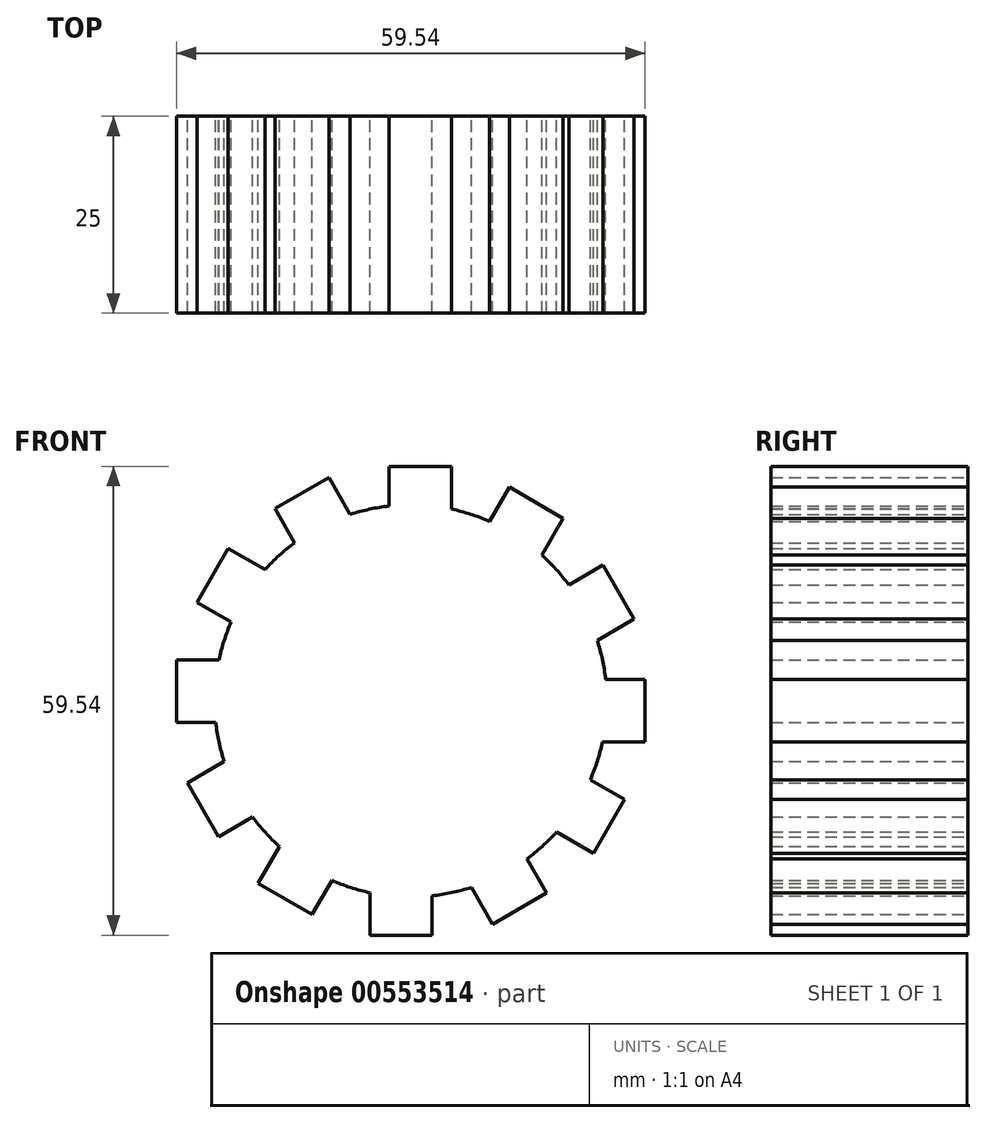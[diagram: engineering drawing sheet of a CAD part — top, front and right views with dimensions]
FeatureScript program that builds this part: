
annotation { "Feature Type Name" : "Feature", "Feature Type Description" : "" }
export const myFeature = defineFeature(function(context is Context, id is Id, definition is map)
    precondition{}
    {
        {
            var Q0;
            Q0=qCreatedBy(makeId("Front.planeOp"),FACE);
            var sketch = newSketch(context, id + "F0", { "sketchPlane" : qUnion([Q0])});
            skCircle(sketch, "E0", {"center": v(0, 0) * mm, "radius": 24.9 * mm});
            skLineSegment(sketch, "E1", {"start": v(-2.73, 24.76) * mm, "end": v(-2.73, 29.77) * mm});
            skLineSegment(sketch, "E2", {"start": v(-2.73, 29.77) * mm, "end": v(5.18, 29.77) * mm});
            skLineSegment(sketch, "E3", {"start": v(5.18, 29.77) * mm, "end": v(5.18, 24.37) * mm});
            skLineSegment(sketch, "E4.1.0", {"start": v(-14.74, 20.08) * mm, "end": v(-17.25, 24.42) * mm});
            skLineSegment(sketch, "E4.1.1", {"start": v(-17.25, 24.42) * mm, "end": v(-10.4, 28.37) * mm});
            skLineSegment(sketch, "E4.1.2", {"start": v(-10.4, 28.37) * mm, "end": v(-7.7, 23.7) * mm});
            skLineSegment(sketch, "E4.2.0", {"start": v(-22.8, 10.02) * mm, "end": v(-27.15, 12.52) * mm});
            skLineSegment(sketch, "E4.2.1", {"start": v(-27.15, 12.52) * mm, "end": v(-23.2, 19.37) * mm});
            skLineSegment(sketch, "E4.2.2", {"start": v(-23.2, 19.37) * mm, "end": v(-18.51, 16.67) * mm});
            skLineSegment(sketch, "E5.1.3.0", {"start": v(-24.76, -2.73) * mm, "end": v(-29.77, -2.73) * mm});
            skLineSegment(sketch, "E5.3.3.0", {"start": v(-29.77, -2.73) * mm, "end": v(-29.77, 5.18) * mm});
            skLineSegment(sketch, "E5.6.3.0", {"start": v(-29.77, 5.18) * mm, "end": v(-24.37, 5.18) * mm});
            skLineSegment(sketch, "E5.1.4.0", {"start": v(-20.08, -14.74) * mm, "end": v(-24.42, -17.25) * mm});
            skLineSegment(sketch, "E5.3.4.0", {"start": v(-24.42, -17.25) * mm, "end": v(-28.37, -10.4) * mm});
            skLineSegment(sketch, "E5.6.4.0", {"start": v(-28.37, -10.4) * mm, "end": v(-23.7, -7.7) * mm});
            skLineSegment(sketch, "E5.1.5.0", {"start": v(-10.02, -22.8) * mm, "end": v(-12.52, -27.15) * mm});
            skLineSegment(sketch, "E5.3.5.0", {"start": v(-12.52, -27.15) * mm, "end": v(-19.37, -23.2) * mm});
            skLineSegment(sketch, "E5.6.5.0", {"start": v(-19.37, -23.2) * mm, "end": v(-16.67, -18.51) * mm});
            skLineSegment(sketch, "E5.1.6.0", {"start": v(2.73, -24.76) * mm, "end": v(2.73, -29.77) * mm});
            skLineSegment(sketch, "E5.3.6.0", {"start": v(2.73, -29.77) * mm, "end": v(-5.18, -29.77) * mm});
            skLineSegment(sketch, "E5.6.6.0", {"start": v(-5.18, -29.77) * mm, "end": v(-5.18, -24.37) * mm});
            skLineSegment(sketch, "E5.1.7.0", {"start": v(14.74, -20.08) * mm, "end": v(17.25, -24.42) * mm});
            skLineSegment(sketch, "E5.3.7.0", {"start": v(17.25, -24.42) * mm, "end": v(10.4, -28.37) * mm});
            skLineSegment(sketch, "E5.6.7.0", {"start": v(10.4, -28.37) * mm, "end": v(7.7, -23.7) * mm});
            skLineSegment(sketch, "E5.1.8.0", {"start": v(22.8, -10.02) * mm, "end": v(27.15, -12.52) * mm});
            skLineSegment(sketch, "E5.3.8.0", {"start": v(27.15, -12.52) * mm, "end": v(23.2, -19.37) * mm});
            skLineSegment(sketch, "E5.6.8.0", {"start": v(23.2, -19.37) * mm, "end": v(18.51, -16.67) * mm});
            skLineSegment(sketch, "E5.1.9.0", {"start": v(24.76, 2.73) * mm, "end": v(29.77, 2.73) * mm});
            skLineSegment(sketch, "E5.3.9.0", {"start": v(29.77, 2.73) * mm, "end": v(29.77, -5.18) * mm});
            skLineSegment(sketch, "E5.6.9.0", {"start": v(29.77, -5.18) * mm, "end": v(24.37, -5.18) * mm});
            skLineSegment(sketch, "E5.1.10.0", {"start": v(20.08, 14.74) * mm, "end": v(24.42, 17.25) * mm});
            skLineSegment(sketch, "E5.3.10.0", {"start": v(24.42, 17.25) * mm, "end": v(28.37, 10.4) * mm});
            skLineSegment(sketch, "E5.6.10.0", {"start": v(28.37, 10.4) * mm, "end": v(23.7, 7.7) * mm});
            skLineSegment(sketch, "E5.1.11.0", {"start": v(10.02, 22.8) * mm, "end": v(12.52, 27.15) * mm});
            skLineSegment(sketch, "E5.3.11.0", {"start": v(12.52, 27.15) * mm, "end": v(19.37, 23.2) * mm});
            skLineSegment(sketch, "E5.6.11.0", {"start": v(19.37, 23.2) * mm, "end": v(16.67, 18.51) * mm});
            skSolve(sketch);
        }
        {
            var Q0;
            Q0 = qSketchRegion(id + "F0", true);
            extrude(context, id + "F1", {"entities" : qUnion([Q0]), "depth" : 25 * mm, "offsetDistance" : 25 * mm});
        }
    });
